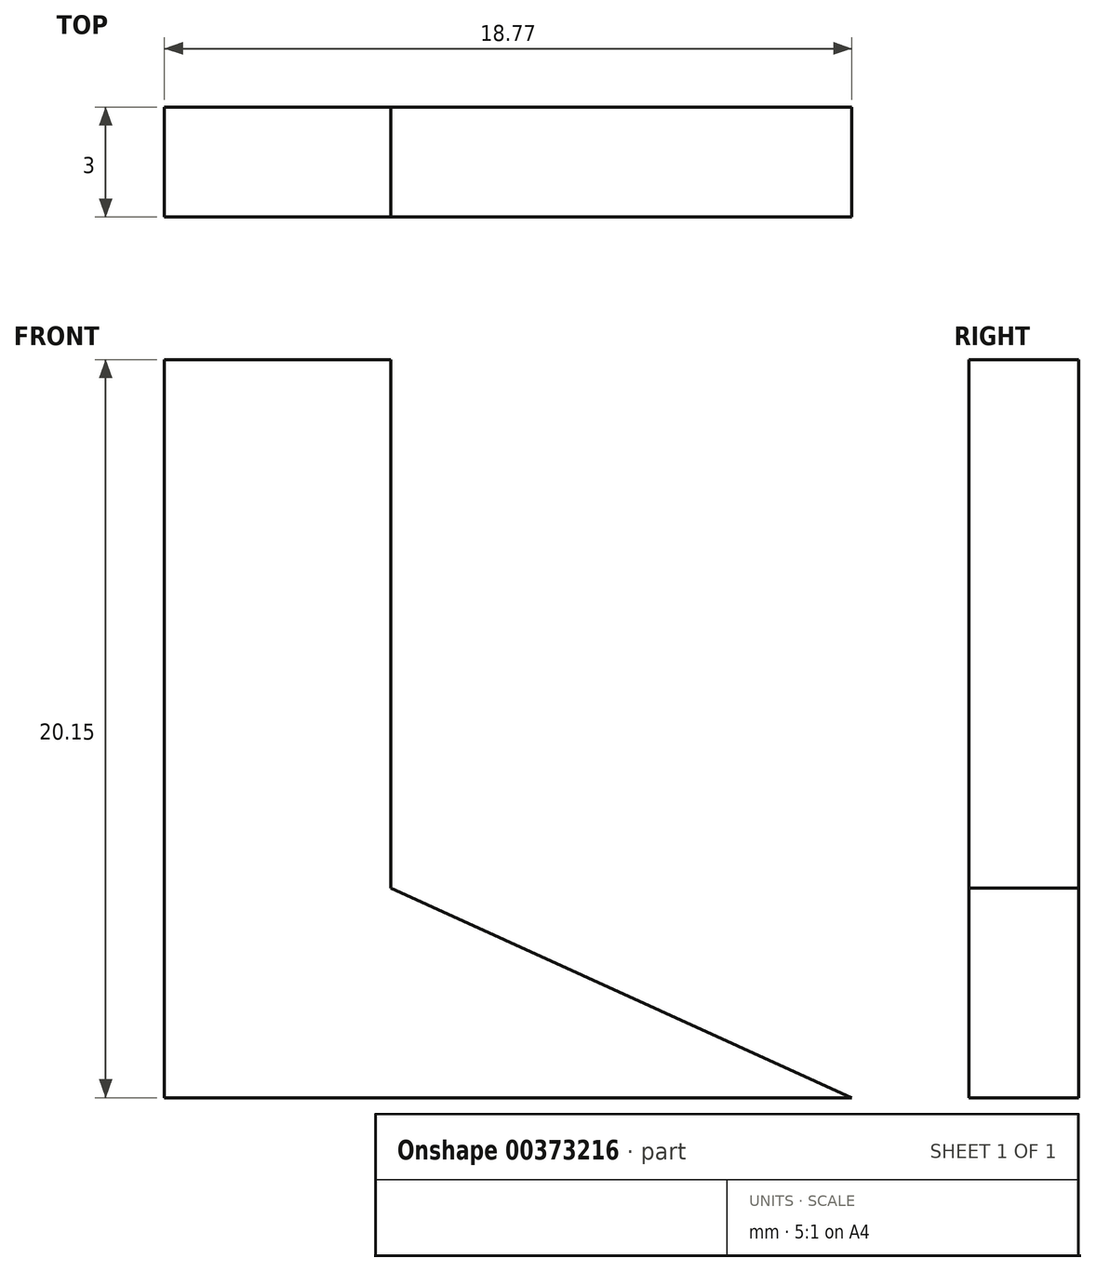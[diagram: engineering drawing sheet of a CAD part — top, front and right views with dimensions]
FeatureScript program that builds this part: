
annotation { "Feature Type Name" : "Feature", "Feature Type Description" : "" }
export const myFeature = defineFeature(function(context is Context, id is Id, definition is map)
    precondition{}
    {
        {
            var Q0;
            Q0=qCreatedBy(makeId("Front.planeOp"),FACE);
            var sketch = newSketch(context, id + "F0", { "sketchPlane" : qUnion([Q0])});
            skLineSegment(sketch, "E0", {"start": v(0, 0) * mm, "end": v(0, 20.15) * mm});
            skLineSegment(sketch, "E1", {"start": v(0, 0) * mm, "end": v(18.77, 0) * mm});
            skLineSegment(sketch, "E2", {"start": v(18.77, 0) * mm, "end": v(6.18, 5.72) * mm});
            skLineSegment(sketch, "E3", {"start": v(6.18, 5.72) * mm, "end": v(6.18, 20.15) * mm});
            skLineSegment(sketch, "E4", {"start": v(0, 20.15) * mm, "end": v(6.18, 20.15) * mm});
            skSolve(sketch);
        }
        {
            var Q0;
            Q0 = qSketchRegion(id + "F0", true);
            extrude(context, id + "F1", {"entities" : qUnion([Q0]), "depth" : 3 * mm});
        }
    });
